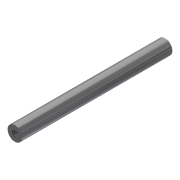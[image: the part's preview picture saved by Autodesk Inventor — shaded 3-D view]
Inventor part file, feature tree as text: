
AUTODESK INVENTOR PART (.ipt)
format: ipt  version: 2015 (Build 190159000, 159)  size: 82,432 bytes
history: native  units: in
note: dims shown in document units (in); Inventor stores cm internally (conversion verified against a paired STEP export)
features: sketch x3, hole x2, extrude x1
ambient origin geometry x8: Origin, YZ Plane, XZ Plane, XY Plane, X Axis, Y Axis, Z Axis, Center Point
bodies: Solid1 (feature_tree)
feature tree (6):
  extrude  "Extrusion1"  Depth=5.18in TaperAngle=0.0deg
  hole  "Hole1"  [1 undecoded]
  hole  "Hole2"  [1 undecoded]
  sketch  "Sketch1"  dims[d0=0.5in d1=5.18in d2=0.0in]
  sketch  "Sketch2"  dims[d3=0.196in d4=1.0in d5=0.375in d6=0.25in d7=0.5635in d8=1.0in d9=0.8108in]
  sketch  "Sketch3"  dims[d10=0.196in d11=1.0in d12=0.375in d13=0.25in d14=0.5635in d15=1.0in d16=0.8108in]
note: 2 required parameter values undecoded (feature->parameter linkage not recoverable at this tier; creation-order binding heuristic only, values carry confidence <= 0.55)
